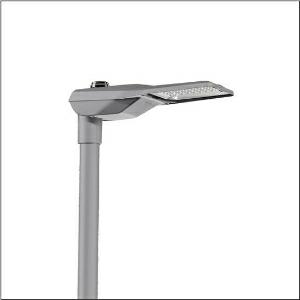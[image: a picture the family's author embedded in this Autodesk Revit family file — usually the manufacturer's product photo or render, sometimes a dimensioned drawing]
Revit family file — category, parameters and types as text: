
# Revit family: streetlight_sl_21_mini___st1_5a_5xe6p47n08gb_4bae
name_source: partatom
category: Lighting Fixtures
units: mm (PartAtom-declared; Revit-internal decimal feet)

## family parameters
Cut with Voids When Loaded = No
Host = Face
Light Source = No
Part Type = Normal
Room Calculation Point = No
Round Connector Dimension = Use Diameter
Shared = No

## types (1)
- --- (1 x LED, 6080 lm, 40.4 W, 4000K)
    Apparent Load = 40 VA
    CIE Flux Codes = 22 53 95 100 100
    Color Rendering = 70
    Color Temperature = 4000K
    Default Elevation = 1800 mm
    Description = Streetlight SL 21 mini, mast luminaire, primary light control with lens, of PMMA, primary optical cover: cover, of toughened safety glass, transparent, light distribution: ST1.5a, light emission: direct distribution, primary light characteristic: asymmetric, installation type: side-entry, LED, 3G 1.5mm², High Power LED, rated luminous flux: 6.080lm, luminous efficacy: 151lm/W, light colour: 740, colour temperature: 4000K, control gear: NEMA (7pin), control: overheat protection, pre-setting: linear dimming characteristic, constant luminous flux control, time-dependent luminous flux control, flexible luminous flux parameterisation, mains connection: 230..240V, AC, 50/60Hz, connection cable pre-assembled, cable length: 8,5m, wiring characteristics: H07RN-F, start of lifetime: 40W, end of service life: 41W, reduction: 19W, luminaire housing, of diecast aluminium (EN AC-44300), powder-coated, SITECO metallic grey (DB 702S), corrosivity category C5 high according to DIN EN ISO 12944, multi-level sealing system, sealing non-destructively replaceable, inclination adjustable: 0°, 5°, 10°, 15°, length: 628mm, width: 235mm, height: 110mm, spigot size: 42mm (side-entry), mounting height: 4..8m, protection rating (complete): IP66, insulation class (complete): insulation class I (protective earthing), certification: CE, ENEC, ENEC+, VDE, impact resistance: IK10, permissible operating ambient temperature for outdoor applications: -40..+50°C, standard-compliant lighting for roads and squares, packaging unit: 1 piece

Light Distribution: ST1.5a
    Height = 110 mm
    Lamp = 1 x LED
    Lamp Light Flux = 6080 lm
    Lamp Power = 40.4 W
    Lamp count = 1
    Length = 625 mm
    Luminous efficacy = 151 lm/W
    Manufacturer = Siteco
    ModVariant = No
    Model = 5XE6P47N08GB
    Number of Poles = 1
    OnlyDefault = Yes
    Power Factor = 1
    Product Name = Streetlight SL 21 mini | ST1.5a
    Product group = mast luminaire | pylon top
    ProductGroupID = 6100
    Protection Class = Protection class I
    Protection Degree = IP 66
    RLX_Detail_Level = 1
    RLX_Emergency_Light_Flux = 0 lm
    RLX_Emergency_Type = 0
    RLX_Emergency_Type_DB = No
    RlxData = <blob elided: 29329 chars, md5=d4f0193f>
    Socket = socket
    Standby Power = 0 W
    System Light Flux = 6080 lm
    System Power = 40 W
    Type Comments = factory setting: luminous flux: 100 % | dim-lin: 254 | 812 mA
    Type Image = l_1294379.jpg
    URL = http://relux.com
    VarID = @adj_133075
    Voltage = 0 V
    Weight = 0.00 kg
    Width = 234 mm

## geometry (parser evidence)
native form markers: Blend x4, Sweep x10
no freeform markers — native parametric forms only
